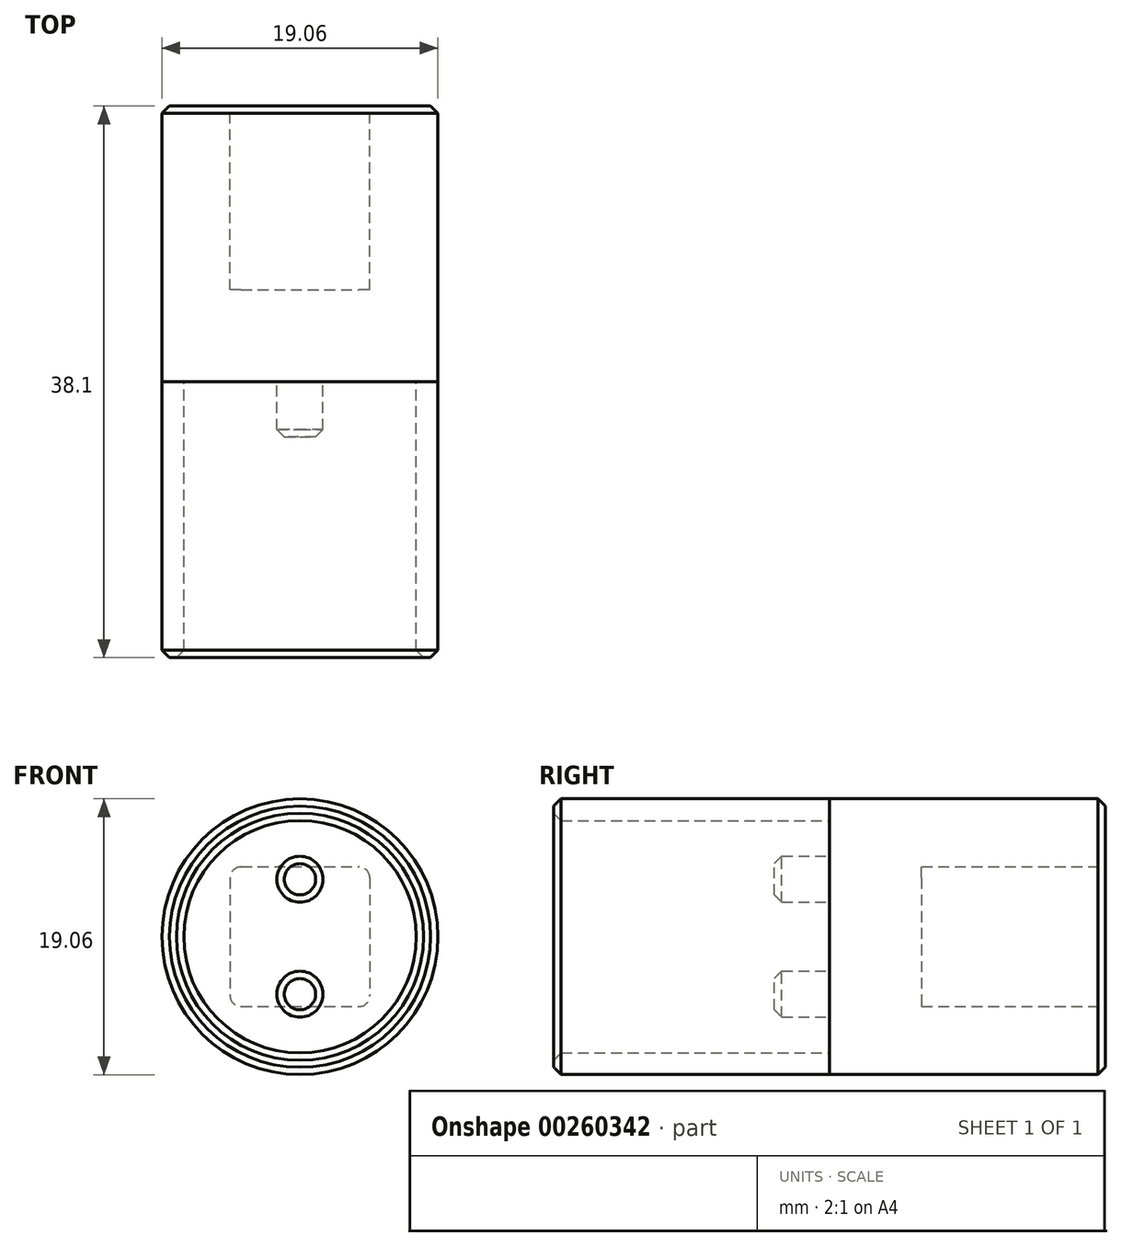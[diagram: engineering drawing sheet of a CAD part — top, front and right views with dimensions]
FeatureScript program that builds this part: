
annotation { "Feature Type Name" : "Feature", "Feature Type Description" : "" }
export const myFeature = defineFeature(function(context is Context, id is Id, definition is map)
    precondition{}
    {
        {
            var Q0;
            Q0=qCreatedBy(makeId("Front.planeOp"),FACE);
            var sketch = newSketch(context, id + "F0", { "sketchPlane" : qUnion([Q0])});
            skCircle(sketch, "E0", {"center": v(0, 0) * mm, "radius": 8 * mm});
            skCircle(sketch, "E1", {"center": v(0, 3.97) * mm, "radius": 1.59 * mm});
            skCircle(sketch, "E2.1.0", {"center": v(0, -3.97) * mm, "radius": 1.59 * mm});
            skSolve(sketch);
        }
        {
            var Q0;
            Q0=makeQuery(id+"F0.imprint","IMPRINT",FACE,{"disambiguationData":[TD([[makeQuery(id+"F0.imprint","IMPRINT",EDGE,{"derivedFrom":sQuery(id+"F0.wireOp",EDGE,"E1")}),1.0]])]});
            var Q1;
            Q1=makeQuery(id+"F0.imprint","IMPRINT",FACE,{"disambiguationData":[TD([[makeQuery(id+"F0.imprint","IMPRINT",EDGE,{"derivedFrom":sQuery(id+"F0.wireOp",EDGE,"E2.1.0")}),1.0]])]});
            extrude(context, id + "F1", {"entities" : qUnion([Q0, Q1]), "depth" : 3.8 * mm});
        }
        {
            var Q0;
            Q0=makeQuery(id+"F0.imprint","IMPRINT",FACE,{"disambiguationData":[TD([[makeQuery(id+"F0.imprint","IMPRINT",EDGE,{"derivedFrom":sQuery(id+"F0.wireOp",EDGE,"E0")}),1.0]])]});
            var sketch = newSketch(context, id + "F2", { "sketchPlane" : qUnion([Q0])});
            skCircle(sketch, "E3", {"center": v(0, 0) * mm, "radius": 8.02 * mm});
            skCircle(sketch, "E4", {"center": v(0, 0) * mm, "radius": 9.53 * mm});
            skSolve(sketch);
        }
        {
            var Q0;
            Q0 = qSketchRegion(id + "F2", true);
            extrude(context, id + "F3", {"entities" : qUnion([Q0]), "depth" : 19.05 * mm});
        }
        {
            var Q0;
            Q0=makeQuery(id+"F3.opExtrude","CAP_FACE",FACE,{"disambiguationData":[OSD([sQuery(id+"F2.wireOp",EDGE,"E3"),sQuery(id+"F2.wireOp",EDGE,"E4")])],"isStart":true});
            var sketch = newSketch(context, id + "F4", { "sketchPlane" : qUnion([Q0])});
            skCircle(sketch, "E5", {"center": v(0, 0) * mm, "radius": 9.53 * mm});
            skSolve(sketch);
        }
        {
            var Q0;
            Q0 = qSketchRegion(id + "F4", true);
            extrude(context, id + "F5", {"entities" : qUnion([Q0]), "depth" : 19.05 * mm});
        }
        {
            var Q0;
            Q0=makeQuery(id+"F5.opExtrude","CAP_FACE",FACE,{"disambiguationData":[OSD([sQuery(id+"F4.wireOp",EDGE,"E5")])],"isStart":false});
            var sketch = newSketch(context, id + "F6", { "sketchPlane" : qUnion([Q0])});
            skLineSegment(sketch, "E6.bottom", {"start": v(4.83, 4.83) * mm, "end": v(-4.83, 4.83) * mm});
            skLineSegment(sketch, "E6.top", {"start": v(4.83, -4.83) * mm, "end": v(-4.83, -4.83) * mm});
            skLineSegment(sketch, "E6.left", {"start": v(4.83, 4.83) * mm, "end": v(4.83, -4.83) * mm});
            skLineSegment(sketch, "E6.right", {"start": v(-4.83, 4.83) * mm, "end": v(-4.83, -4.83) * mm});
            skPoint(sketch, "E6.middle", {"position": v(0, 0) * mm});
            skSolve(sketch);
        }
        {
            var Q0;
            Q0 = qSketchRegion(id + "F6", true);
            extrude(context, id + "F7", {"entities" : qUnion([Q0]), "operationType" : NewBodyOperationType.REMOVE, "oppositeDirection" : true, "depth" : 12.7 * mm});
        }
        {
            var Q0;
            Q0=makeQuery(id+"F7.boolean.opBoolean","COPY",EDGE,{"derivedFrom":makeQuery(id+"F7.opExtrude","SWEPT_EDGE",EDGE,{"disambiguationData":[OSD([sQuery(id+"F6.wireOp",EDGE,"E6.top"),sQuery(id+"F6.wireOp",EDGE,"E6.left")])]})});
            var Q1;
            Q1=makeQuery(id+"F7.boolean.opBoolean","COPY",EDGE,{"derivedFrom":makeQuery(id+"F7.opExtrude","SWEPT_EDGE",EDGE,{"disambiguationData":[OSD([sQuery(id+"F6.wireOp",EDGE,"E6.bottom"),sQuery(id+"F6.wireOp",EDGE,"E6.left")])]})});
            var Q2;
            Q2=makeQuery(id+"F7.boolean.opBoolean","COPY",EDGE,{"derivedFrom":makeQuery(id+"F7.opExtrude","SWEPT_EDGE",EDGE,{"disambiguationData":[OSD([sQuery(id+"F6.wireOp",EDGE,"E6.bottom"),sQuery(id+"F6.wireOp",EDGE,"E6.right")])]})});
            var Q3;
            Q3=makeQuery(id+"F7.boolean.opBoolean","COPY",EDGE,{"derivedFrom":makeQuery(id+"F7.opExtrude","SWEPT_EDGE",EDGE,{"disambiguationData":[OSD([sQuery(id+"F6.wireOp",EDGE,"E6.top"),sQuery(id+"F6.wireOp",EDGE,"E6.right")])]})});
            fillet(context, id + "F8", {"entities" : qUnion([Q0, Q1, Q2, Q3]), "radius" : 0.76 * mm, "tangentPropagation" : true, "allowEdgeOverflow" : false});
        }
        {
            var Q0;
            Q0=makeQuery(id+"F7.boolean.opBoolean","COPY",EDGE,{"derivedFrom":makeQuery(id+"F7.opExtrude","CAP_EDGE",EDGE,{"disambiguationData":[OSD([sQuery(id+"F6.wireOp",EDGE,"E6.top")])],"isStart":true})});
            var Q1;
            Q1=makeQuery(id+"F5.opExtrude","CAP_EDGE",EDGE,{"disambiguationData":[OSD([sQuery(id+"F4.wireOp",EDGE,"E5")])],"isStart":false});
            var Q2;
            Q2=makeQuery(id+"F3.opExtrude","CAP_EDGE",EDGE,{"disambiguationData":[OSD([sQuery(id+"F2.wireOp",EDGE,"E4")])],"isStart":false});
            var Q3;
            Q3=makeQuery(id+"F3.opExtrude","CAP_EDGE",EDGE,{"disambiguationData":[OSD([sQuery(id+"F2.wireOp",EDGE,"E3")])],"isStart":false});
            var Q4;
            Q4=makeQuery(id+"F1.opExtrude","CAP_EDGE",EDGE,{"disambiguationData":[OSD([sQuery(id+"F0.wireOp",EDGE,"E1")])],"isStart":false});
            var Q5;
            Q5=makeQuery(id+"F1.opExtrude","CAP_EDGE",EDGE,{"disambiguationData":[OSD([sQuery(id+"F0.wireOp",EDGE,"E2.1.0")])],"isStart":false});
            chamfer(context, id + "F9", {"entities" : qUnion([Q0, Q1, Q2, Q3, Q4, Q5]), "width" : 0.5 * mm, "tangentPropagation" : true});
        }
    });
